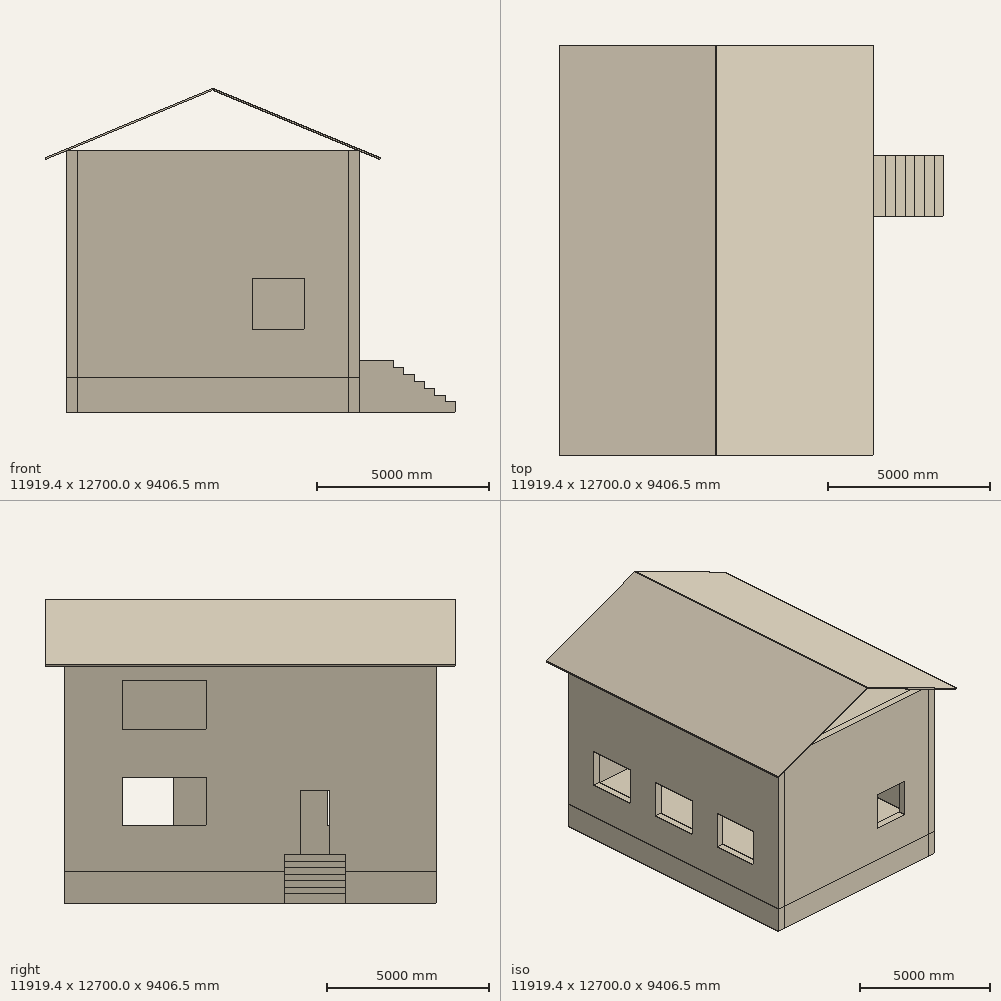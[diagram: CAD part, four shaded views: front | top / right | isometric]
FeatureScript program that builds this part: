
annotation { "Feature Type Name" : "Feature", "Feature Type Description" : "" }
export const myFeature = defineFeature(function(context is Context, id is Id, definition is map)
    precondition{}
    {
        {
            var Q0;
            Q0=qCreatedBy(makeId("Front.planeOp"),FACE);
            var sketch = newSketch(context, id + "F0", { "sketchPlane" : qUnion([Q0])});
            skLineSegment(sketch, "E0.bottom", {"start": v(0, 0) * mm, "end": v(300, 0) * mm});
            skLineSegment(sketch, "E0.top", {"start": v(0, 1000) * mm, "end": v(300, 1000) * mm});
            skLineSegment(sketch, "E0.left", {"start": v(0, 0) * mm, "end": v(0, 1000) * mm});
            skLineSegment(sketch, "E0.right", {"start": v(300, 0) * mm, "end": v(300, 1000) * mm});
            skSolve(sketch);
        }
        {
            var Q0;
            Q0 = qSketchRegion(id + "F0", true);
            extrude(context, id + "F1", {"entities" : qUnion([Q0]), "oppositeDirection" : true, "depth" : 11500 * mm});
        }
        {
            var Q0;
            Q0=makeQuery(id+"F1.opExtrude","SWEPT_BODY",BODY,{"disambiguationData":[OSD([sQuery(id+"F0.wireOp",EDGE,"E0.bottom"),sQuery(id+"F0.wireOp",EDGE,"E0.top"),sQuery(id+"F0.wireOp",EDGE,"E0.left"),sQuery(id+"F0.wireOp",EDGE,"E0.right")])]});
            transform(context, id + "F2", {"entities" : qUnion([Q0]), "transformType" : TransformType.TRANSLATION_3D, "dx" : 8200 * mm, "dy" : 0 * mm, "dz" : 0 * mm, "makeCopy" : true});
        }
        {
            var Q0;
            Q0=makeQuery(id+"F1.opExtrude","SWEPT_FACE",FACE,{"disambiguationData":[OSD([sQuery(id+"F0.wireOp",EDGE,"E0.right")])]});
            var sketch = newSketch(context, id + "F3", { "sketchPlane" : qUnion([Q0])});
            skLineSegment(sketch, "E1.bottom", {"start": v(0, 0) * mm, "end": v(300, 0) * mm});
            skLineSegment(sketch, "E1.top", {"start": v(0, 1000) * mm, "end": v(300, 1000) * mm});
            skLineSegment(sketch, "E1.left", {"start": v(0, 0) * mm, "end": v(0, 1000) * mm});
            skLineSegment(sketch, "E1.right", {"start": v(300, 0) * mm, "end": v(300, 1000) * mm});
            skSolve(sketch);
        }
        {
            var Q0;
            Q0 = qSketchRegion(id + "F3", true);
            extrude(context, id + "F4", {"entities" : qUnion([Q0]), "depth" : 7900 * mm});
        }
        {
            var Q0;
            Q0=makeQuery(id+"F4.opExtrude","SWEPT_BODY",BODY,{"disambiguationData":[OSD([sQuery(id+"F3.wireOp",EDGE,"E1.bottom"),sQuery(id+"F3.wireOp",EDGE,"E1.top"),sQuery(id+"F3.wireOp",EDGE,"E1.left"),sQuery(id+"F3.wireOp",EDGE,"E1.right")])]});
            transform(context, id + "F5", {"entities" : qUnion([Q0]), "transformType" : TransformType.TRANSLATION_3D, "dx" : 0 * mm, "dy" : 11200 * mm, "dz" : 0 * mm, "makeCopy" : true});
        }
        {
            var Q0;
            Q0=makeQuery(id+"F1.opExtrude","CAP_FACE",FACE,{"disambiguationData":[OSD([sQuery(id+"F0.wireOp",EDGE,"E0.bottom"),sQuery(id+"F0.wireOp",EDGE,"E0.top"),sQuery(id+"F0.wireOp",EDGE,"E0.left"),sQuery(id+"F0.wireOp",EDGE,"E0.right")])],"isStart":true});
            var sketch = newSketch(context, id + "F6", { "sketchPlane" : qUnion([Q0])});
            skLineSegment(sketch, "E2.bottom", {"start": v(0, 1000) * mm, "end": v(300, 1000) * mm});
            skLineSegment(sketch, "E2.top", {"start": v(0, 7600) * mm, "end": v(300, 7600) * mm});
            skLineSegment(sketch, "E2.left", {"start": v(0, 1000) * mm, "end": v(0, 7600) * mm});
            skLineSegment(sketch, "E2.right", {"start": v(300, 1000) * mm, "end": v(300, 7600) * mm});
            skSolve(sketch);
        }
        {
            var Q0;
            Q0=makeQuery(id+"F6.imprint","IMPRINT",FACE,{"disambiguationData":[TD([[makeQuery(id+"F6.imprint","IMPRINT",EDGE,{"derivedFrom":sQuery(id+"F6.wireOp",EDGE,"E2.bottom")}),1.0]])]});
            extrude(context, id + "F7", {"entities" : qUnion([Q0]), "oppositeDirection" : true, "depth" : 11500 * mm});
        }
        {
            var Q0;
            Q0=makeQuery(id+"F7.opExtrude","SWEPT_BODY",BODY,{"disambiguationData":[OSD([sQuery(id+"F6.wireOp",EDGE,"E2.bottom"),sQuery(id+"F6.wireOp",EDGE,"E2.top"),sQuery(id+"F6.wireOp",EDGE,"E2.left"),sQuery(id+"F6.wireOp",EDGE,"E2.right")])]});
            transform(context, id + "F8", {"entities" : qUnion([Q0]), "transformType" : TransformType.TRANSLATION_3D, "dx" : 8200 * mm, "dy" : 0 * mm, "dz" : 0 * mm, "makeCopy" : true});
        }
        {
            var Q0;
            Q0=makeQuery(id+"F7.opExtrude","SWEPT_FACE",FACE,{"disambiguationData":[OSD([sQuery(id+"F6.wireOp",EDGE,"E2.right")])]});
            var sketch = newSketch(context, id + "F9", { "sketchPlane" : qUnion([Q0])});
            skLineSegment(sketch, "E3.bottom", {"start": v(0, 1000) * mm, "end": v(300, 1000) * mm});
            skLineSegment(sketch, "E3.top", {"start": v(0, 7600) * mm, "end": v(300, 7600) * mm});
            skLineSegment(sketch, "E3.left", {"start": v(0, 1000) * mm, "end": v(0, 7600) * mm});
            skLineSegment(sketch, "E3.right", {"start": v(300, 1000) * mm, "end": v(300, 7600) * mm});
            skSolve(sketch);
        }
        {
            var Q0;
            Q0 = qSketchRegion(id + "F9", true);
            extrude(context, id + "F10", {"entities" : qUnion([Q0]), "depth" : 7900 * mm});
        }
        {
            var Q0;
            Q0=makeQuery(id+"F10.opExtrude","SWEPT_BODY",BODY,{"disambiguationData":[OSD([sQuery(id+"F9.wireOp",EDGE,"E3.bottom"),sQuery(id+"F9.wireOp",EDGE,"E3.top"),sQuery(id+"F9.wireOp",EDGE,"E3.left"),sQuery(id+"F9.wireOp",EDGE,"E3.right")])]});
            transform(context, id + "F11", {"entities" : qUnion([Q0]), "transformType" : TransformType.TRANSLATION_3D, "dx" : 0 * mm, "dy" : 11200 * mm, "dz" : 0 * mm, "makeCopy" : true});
        }
        {
            var Q0;
            Q0=makeQuery(id+"F8.opPattern","COPY",FACE,{"derivedFrom":makeQuery(id+"F7.opExtrude","SWEPT_FACE",FACE,{"disambiguationData":[OSD([sQuery(id+"F6.wireOp",EDGE,"E2.right")])]}),"instanceName":"1"});
            var sketch = newSketch(context, id + "F12", { "sketchPlane" : qUnion([Q0])});
            skLineSegment(sketch, "E4.bottom", {"start": v(0, 7600) * mm, "end": v(12700, 7600) * mm});
            skLineSegment(sketch, "E4.top", {"start": v(0, 7550) * mm, "end": v(12700, 7550) * mm});
            skLineSegment(sketch, "E4.left", {"start": v(0, 7600) * mm, "end": v(0, 7550) * mm});
            skLineSegment(sketch, "E4.right", {"start": v(12700, 7600) * mm, "end": v(12700, 7550) * mm});
            skSolve(sketch);
        }
        {
            var Q0;
            Q0 = qSketchRegion(id + "F12", true);
            extrude(context, id + "F13", {"entities" : qUnion([Q0]), "depth" : 650 * mm});
        }
        {
            var Q0;
            Q0=makeQuery(id+"F13.opExtrude","SWEPT_BODY",BODY,{"disambiguationData":[OSD([sQuery(id+"F12.wireOp",EDGE,"E4.bottom"),sQuery(id+"F12.wireOp",EDGE,"E4.top"),sQuery(id+"F12.wireOp",EDGE,"E4.left"),sQuery(id+"F12.wireOp",EDGE,"E4.right")])]});
            transform(context, id + "F14", {"entities" : qUnion([Q0]), "transformType" : TransformType.TRANSLATION_3D, "dx" : 0 * mm, "dy" : -600 * mm, "dz" : 0 * mm, "makeCopy" : false});
        }
        {
            var Q0;
            Q0=makeQuery(id+"F13.opExtrude","SWEPT_BODY",BODY,{"disambiguationData":[OSD([sQuery(id+"F12.wireOp",EDGE,"E4.bottom"),sQuery(id+"F12.wireOp",EDGE,"E4.top"),sQuery(id+"F12.wireOp",EDGE,"E4.left"),sQuery(id+"F12.wireOp",EDGE,"E4.right")])]});
            transform(context, id + "F15", {"entities" : qUnion([Q0]), "transformType" : TransformType.TRANSLATION_3D, "dx" : 0 * mm, "dy" : 0 * mm, "dz" : 50 * mm, "makeCopy" : false});
        }
        {
            var Q0;
            Q0=makeQuery(id+"F13.opExtrude","SWEPT_BODY",BODY,{"disambiguationData":[OSD([sQuery(id+"F12.wireOp",EDGE,"E4.bottom"),sQuery(id+"F12.wireOp",EDGE,"E4.top"),sQuery(id+"F12.wireOp",EDGE,"E4.left"),sQuery(id+"F12.wireOp",EDGE,"E4.right")])]});
            var Q1;
            Q1=makeQuery(id+"F8.opPattern","COPY",EDGE,{"derivedFrom":makeQuery(id+"F7.opExtrude","SWEPT_EDGE",EDGE,{"disambiguationData":[OSD([sQuery(id+"F6.wireOp",EDGE,"E2.top"),sQuery(id+"F6.wireOp",EDGE,"E2.right")])]}),"instanceName":"1"});
            transform(context, id + "F16", {"entities" : qUnion([Q0]), "transformType" : TransformType.ROTATION, "transformAxis" : qUnion([Q1]), "angle" : 22.5 * degree, "oppositeDirection" : true, "makeCopy" : false});
        }
        {
            var Q0;
            Q0=makeQuery(id+"F13.opExtrude","CAP_FACE",FACE,{"disambiguationData":[OSD([sQuery(id+"F12.wireOp",EDGE,"E4.bottom"),sQuery(id+"F12.wireOp",EDGE,"E4.top"),sQuery(id+"F12.wireOp",EDGE,"E4.left"),sQuery(id+"F12.wireOp",EDGE,"E4.right")])],"isStart":true});
            extrude(context, id + "F17", {"entities" : qUnion([Q0]), "operationType" : NewBodyOperationType.ADD, "depth" : 4600 * mm});
        }
        {
            var Q0;
            Q0=makeQuery(id+"F13.opExtrude","SWEPT_BODY",BODY,{"disambiguationData":[OSD([sQuery(id+"F12.wireOp",EDGE,"E4.bottom"),sQuery(id+"F12.wireOp",EDGE,"E4.top"),sQuery(id+"F12.wireOp",EDGE,"E4.left"),sQuery(id+"F12.wireOp",EDGE,"E4.right")])]});
            var Q1;
            {var subQ0=sQuery(id+"F12.wireOp",EDGE,"E4.right");var subQ1=sQuery(id+"F12.wireOp",EDGE,"E4.bottom");Q1=makeQuery(id+"F17.boolean.opBoolean","MERGE",EDGE,{"derivedFrom":[makeQuery(id+"F13.opExtrude","SWEPT_EDGE",EDGE,{"disambiguationData":[OSD([subQ1,subQ0])]}),makeQuery(id+"F17.opExtrude","SWEPT_EDGE",EDGE,{"disambiguationData":[OSD([subQ1,subQ0])]})]});}
            transform(context, id + "F18", {"entities" : qUnion([Q0]), "transformType" : TransformType.TRANSLATION_ENTITY, "oppositeDirectionEntity" : false, "transformLine" : qUnion([Q1]), "makeCopy" : true});
        }
        {
            var Q0;
            Q0=makeQuery(id+"F18.opPattern","COPY",BODY,{"derivedFrom":makeQuery(id+"F13.opExtrude","SWEPT_BODY",BODY,{"disambiguationData":[OSD([sQuery(id+"F12.wireOp",EDGE,"E4.bottom"),sQuery(id+"F12.wireOp",EDGE,"E4.top"),sQuery(id+"F12.wireOp",EDGE,"E4.left"),sQuery(id+"F12.wireOp",EDGE,"E4.right")])]}),"instanceName":"1"});
            var Q1;
            Q1=makeQuery(id+"F17.opExtrude","CAP_EDGE",EDGE,{"disambiguationData":[OSD([sQuery(id+"F12.wireOp",EDGE,"E4.top")])],"isStart":false});
            transform(context, id + "F19", {"entities" : qUnion([Q0]), "transformType" : TransformType.ROTATION, "transformAxis" : qUnion([Q1]), "angle" : 45 * degree, "oppositeDirection" : true, "makeCopy" : false});
        }
        {
            var Q0;
            Q0=makeQuery(id+"F8.opPattern","COPY",FACE,{"derivedFrom":makeQuery(id+"F7.opExtrude","SWEPT_FACE",FACE,{"disambiguationData":[OSD([sQuery(id+"F6.wireOp",EDGE,"E2.right")])]}),"instanceName":"1"});
            var sketch = newSketch(context, id + "F20", { "sketchPlane" : qUnion([Q0])});
            skLineSegment(sketch, "E5.bottom", {"start": v(0, 1000) * mm, "end": v(1800, 1000) * mm});
            skLineSegment(sketch, "E5.top", {"start": v(0, 2400) * mm, "end": v(1800, 2400) * mm});
            skLineSegment(sketch, "E5.left", {"start": v(0, 1000) * mm, "end": v(0, 2400) * mm});
            skLineSegment(sketch, "E5.right", {"start": v(1800, 1000) * mm, "end": v(1800, 2400) * mm});
            skSolve(sketch);
        }
        {
            var Q0;
            Q0 = qSketchRegion(id + "F20", true);
            extrude(context, id + "F21", {"entities" : qUnion([Q0]), "depth" : 25 * mm});
        }
        {
            var Q0;
            Q0=makeQuery(id+"F21.opExtrude","CAP_FACE",FACE,{"disambiguationData":[OSD([sQuery(id+"F20.wireOp",EDGE,"E5.bottom"),sQuery(id+"F20.wireOp",EDGE,"E5.top"),sQuery(id+"F20.wireOp",EDGE,"E5.left"),sQuery(id+"F20.wireOp",EDGE,"E5.right")])],"isStart":false});
            var sketch = newSketch(context, id + "F22", { "sketchPlane" : qUnion([Q0])});
            skLineSegment(sketch, "E6.bottom", {"start": v(1800, 2400) * mm, "end": v(4400, 2400) * mm});
            skLineSegment(sketch, "E6.top", {"start": v(1800, 3900) * mm, "end": v(4400, 3900) * mm});
            skLineSegment(sketch, "E6.left", {"start": v(1800, 2400) * mm, "end": v(1800, 3900) * mm});
            skLineSegment(sketch, "E6.right", {"start": v(4400, 2400) * mm, "end": v(4400, 3900) * mm});
            skSolve(sketch);
        }
        {
            var Q0;
            Q0=makeQuery(id+"F22.imprint","IMPRINT",FACE,{"disambiguationData":[TD([[makeQuery(id+"F22.imprint","IMPRINT",EDGE,{"derivedFrom":sQuery(id+"F22.wireOp",EDGE,"E6.bottom")}),1.0]])]});
            extrude(context, id + "F23", {"entities" : qUnion([Q0]), "operationType" : NewBodyOperationType.REMOVE, "oppositeDirection" : true, "depth" : 500 * mm});
        }
        {
            var Q0;
            Q0=makeQuery(id+"F21.opExtrude","SWEPT_BODY",BODY,{"disambiguationData":[OSD([sQuery(id+"F20.wireOp",EDGE,"E5.bottom"),sQuery(id+"F20.wireOp",EDGE,"E5.top"),sQuery(id+"F20.wireOp",EDGE,"E5.left"),sQuery(id+"F20.wireOp",EDGE,"E5.right")])]});
            deleteBodies(context, id + "F24", {"entities" : qUnion([Q0])});
        }
        {
            var Q0;
            Q0=makeQuery(id+"F8.opPattern","COPY",FACE,{"derivedFrom":makeQuery(id+"F7.opExtrude","SWEPT_FACE",FACE,{"disambiguationData":[OSD([sQuery(id+"F6.wireOp",EDGE,"E2.right")])]}),"instanceName":"1"});
            var sketch = newSketch(context, id + "F25", { "sketchPlane" : qUnion([Q0])});
            skLineSegment(sketch, "E7.bottom", {"start": v(0, 1000) * mm, "end": v(7300, 1000) * mm});
            skLineSegment(sketch, "E7.top", {"start": v(0, 1500) * mm, "end": v(7300, 1500) * mm});
            skLineSegment(sketch, "E7.left", {"start": v(0, 1000) * mm, "end": v(0, 1500) * mm});
            skLineSegment(sketch, "E7.right", {"start": v(7300, 1000) * mm, "end": v(7300, 1500) * mm});
            skSolve(sketch);
        }
        {
            var Q0;
            Q0 = qSketchRegion(id + "F25", true);
            extrude(context, id + "F26", {"entities" : qUnion([Q0]), "depth" : 25 * mm});
        }
        {
            var Q0;
            Q0=makeQuery(id+"F26.opExtrude","CAP_FACE",FACE,{"disambiguationData":[OSD([sQuery(id+"F25.wireOp",EDGE,"E7.bottom"),sQuery(id+"F25.wireOp",EDGE,"E7.top"),sQuery(id+"F25.wireOp",EDGE,"E7.left"),sQuery(id+"F25.wireOp",EDGE,"E7.right")])],"isStart":false});
            var sketch = newSketch(context, id + "F27", { "sketchPlane" : qUnion([Q0])});
            skLineSegment(sketch, "E8.bottom", {"start": v(7300, 1500) * mm, "end": v(8200, 1500) * mm});
            skLineSegment(sketch, "E8.top", {"start": v(7300, 3500) * mm, "end": v(8200, 3500) * mm});
            skLineSegment(sketch, "E8.left", {"start": v(7300, 1500) * mm, "end": v(7300, 3500) * mm});
            skLineSegment(sketch, "E8.right", {"start": v(8200, 1500) * mm, "end": v(8200, 3500) * mm});
            skSolve(sketch);
        }
        {
            var Q0;
            Q0=makeQuery(id+"F27.imprint","IMPRINT",FACE,{"disambiguationData":[TD([[makeQuery(id+"F27.imprint","IMPRINT",EDGE,{"derivedFrom":sQuery(id+"F27.wireOp",EDGE,"E8.bottom")}),1.0]])]});
            extrude(context, id + "F28", {"entities" : qUnion([Q0]), "operationType" : NewBodyOperationType.REMOVE, "oppositeDirection" : true, "depth" : 500 * mm});
        }
        {
            var Q0;
            Q0=makeQuery(id+"F26.opExtrude","SWEPT_BODY",BODY,{"disambiguationData":[OSD([sQuery(id+"F25.wireOp",EDGE,"E7.bottom"),sQuery(id+"F25.wireOp",EDGE,"E7.top"),sQuery(id+"F25.wireOp",EDGE,"E7.left"),sQuery(id+"F25.wireOp",EDGE,"E7.right")])]});
            deleteBodies(context, id + "F29", {"entities" : qUnion([Q0])});
        }
        {
            var Q0;
            Q0=makeQuery(id+"F8.opPattern","COPY",FACE,{"derivedFrom":makeQuery(id+"F7.opExtrude","SWEPT_FACE",FACE,{"disambiguationData":[OSD([sQuery(id+"F6.wireOp",EDGE,"E2.right")])]}),"instanceName":"1"});
            var sketch = newSketch(context, id + "F30", { "sketchPlane" : qUnion([Q0])});
            skLineSegment(sketch, "E9.bottom", {"start": v(7300, 1500) * mm, "end": v(9200, 1500) * mm});
            skLineSegment(sketch, "E9.top", {"start": v(7300, 0) * mm, "end": v(9200, 0) * mm});
            skLineSegment(sketch, "E9.left", {"start": v(7300, 1500) * mm, "end": v(7300, 0) * mm});
            skLineSegment(sketch, "E9.right", {"start": v(9200, 1500) * mm, "end": v(9200, 0) * mm});
            skSolve(sketch);
        }
        {
            var Q0;
            Q0 = qSketchRegion(id + "F30", true);
            extrude(context, id + "F31", {"entities" : qUnion([Q0]), "depth" : 1000 * mm});
        }
        {
            var Q0;
            Q0=makeQuery(id+"F31.opExtrude","SWEPT_BODY",BODY,{"disambiguationData":[OSD([sQuery(id+"F30.wireOp",EDGE,"E9.bottom"),sQuery(id+"F30.wireOp",EDGE,"E9.top"),sQuery(id+"F30.wireOp",EDGE,"E9.left"),sQuery(id+"F30.wireOp",EDGE,"E9.right")])]});
            transform(context, id + "F32", {"entities" : qUnion([Q0]), "transformType" : TransformType.TRANSLATION_3D, "dx" : 0 * mm, "dy" : -500 * mm, "dz" : 0 * mm, "makeCopy" : false});
        }
        {
            var Q0;
            Q0=makeQuery(id+"F31.opExtrude","CAP_FACE",FACE,{"disambiguationData":[OSD([sQuery(id+"F30.wireOp",EDGE,"E9.bottom"),sQuery(id+"F30.wireOp",EDGE,"E9.top"),sQuery(id+"F30.wireOp",EDGE,"E9.left"),sQuery(id+"F30.wireOp",EDGE,"E9.right")])],"isStart":false});
            var sketch = newSketch(context, id + "F33", { "sketchPlane" : qUnion([Q0])});
            skLineSegment(sketch, "E10.bottom", {"start": v(6800, 0) * mm, "end": v(8700, 0) * mm});
            skLineSegment(sketch, "E10.top", {"start": v(6800, 1300) * mm, "end": v(8700, 1300) * mm});
            skLineSegment(sketch, "E10.left", {"start": v(6800, 0) * mm, "end": v(6800, 1300) * mm});
            skLineSegment(sketch, "E10.right", {"start": v(8700, 0) * mm, "end": v(8700, 1300) * mm});
            skSolve(sketch);
        }
        {
            var Q0;
            Q0 = qSketchRegion(id + "F33", true);
            extrude(context, id + "F34", {"entities" : qUnion([Q0]), "operationType" : NewBodyOperationType.ADD, "depth" : 300 * mm});
        }
        {
            var Q0;
            Q0=makeQuery(id+"F34.opExtrude","CAP_FACE",FACE,{"disambiguationData":[OSD([sQuery(id+"F33.wireOp",EDGE,"E10.bottom"),sQuery(id+"F33.wireOp",EDGE,"E10.top"),sQuery(id+"F33.wireOp",EDGE,"E10.left"),sQuery(id+"F33.wireOp",EDGE,"E10.right")])],"isStart":false});
            var sketch = newSketch(context, id + "F35", { "sketchPlane" : qUnion([Q0])});
            skLineSegment(sketch, "E11.bottom", {"start": v(6800, 0) * mm, "end": v(8700, 0) * mm});
            skLineSegment(sketch, "E11.top", {"start": v(6800, 1100) * mm, "end": v(8700, 1100) * mm});
            skLineSegment(sketch, "E11.left", {"start": v(6800, 0) * mm, "end": v(6800, 1100) * mm});
            skLineSegment(sketch, "E11.right", {"start": v(8700, 0) * mm, "end": v(8700, 1100) * mm});
            skSolve(sketch);
        }
        {
            var Q0;
            Q0 = qSketchRegion(id + "F35", true);
            extrude(context, id + "F36", {"entities" : qUnion([Q0]), "operationType" : NewBodyOperationType.ADD, "depth" : 300 * mm});
        }
        {
            var Q0;
            Q0=makeQuery(id+"F36.opExtrude","CAP_FACE",FACE,{"disambiguationData":[OSD([sQuery(id+"F35.wireOp",EDGE,"E11.bottom"),sQuery(id+"F35.wireOp",EDGE,"E11.top"),sQuery(id+"F35.wireOp",EDGE,"E11.left"),sQuery(id+"F35.wireOp",EDGE,"E11.right")])],"isStart":false});
            var sketch = newSketch(context, id + "F37", { "sketchPlane" : qUnion([Q0])});
            skLineSegment(sketch, "E12.bottom", {"start": v(6800, 0) * mm, "end": v(8700, 0) * mm});
            skLineSegment(sketch, "E12.top", {"start": v(6800, 900) * mm, "end": v(8700, 900) * mm});
            skLineSegment(sketch, "E12.left", {"start": v(6800, 0) * mm, "end": v(6800, 900) * mm});
            skLineSegment(sketch, "E12.right", {"start": v(8700, 0) * mm, "end": v(8700, 900) * mm});
            skSolve(sketch);
        }
        {
            var Q0;
            Q0 = qSketchRegion(id + "F37", true);
            extrude(context, id + "F38", {"entities" : qUnion([Q0]), "operationType" : NewBodyOperationType.ADD, "depth" : 300 * mm});
        }
        {
            var Q0;
            Q0=makeQuery(id+"F38.opExtrude","CAP_FACE",FACE,{"disambiguationData":[OSD([sQuery(id+"F37.wireOp",EDGE,"E12.bottom"),sQuery(id+"F37.wireOp",EDGE,"E12.top"),sQuery(id+"F37.wireOp",EDGE,"E12.left"),sQuery(id+"F37.wireOp",EDGE,"E12.right")])],"isStart":false});
            var sketch = newSketch(context, id + "F39", { "sketchPlane" : qUnion([Q0])});
            skLineSegment(sketch, "E13.bottom", {"start": v(6800, 0) * mm, "end": v(8700, 0) * mm});
            skLineSegment(sketch, "E13.top", {"start": v(6800, 700) * mm, "end": v(8700, 700) * mm});
            skLineSegment(sketch, "E13.left", {"start": v(6800, 0) * mm, "end": v(6800, 700) * mm});
            skLineSegment(sketch, "E13.right", {"start": v(8700, 0) * mm, "end": v(8700, 700) * mm});
            skSolve(sketch);
        }
        {
            var Q0;
            Q0 = qSketchRegion(id + "F39", true);
            extrude(context, id + "F40", {"entities" : qUnion([Q0]), "operationType" : NewBodyOperationType.ADD, "depth" : 300 * mm});
        }
        {
            var Q0;
            Q0=makeQuery(id+"F40.opExtrude","CAP_FACE",FACE,{"disambiguationData":[OSD([sQuery(id+"F39.wireOp",EDGE,"E13.bottom"),sQuery(id+"F39.wireOp",EDGE,"E13.top"),sQuery(id+"F39.wireOp",EDGE,"E13.left"),sQuery(id+"F39.wireOp",EDGE,"E13.right")])],"isStart":false});
            var sketch = newSketch(context, id + "F41", { "sketchPlane" : qUnion([Q0])});
            skLineSegment(sketch, "E14.bottom", {"start": v(6800, 0) * mm, "end": v(8700, 0) * mm});
            skLineSegment(sketch, "E14.top", {"start": v(6800, 500) * mm, "end": v(8700, 500) * mm});
            skLineSegment(sketch, "E14.left", {"start": v(6800, 0) * mm, "end": v(6800, 500) * mm});
            skLineSegment(sketch, "E14.right", {"start": v(8700, 0) * mm, "end": v(8700, 500) * mm});
            skSolve(sketch);
        }
        {
            var Q0;
            Q0 = qSketchRegion(id + "F41", true);
            extrude(context, id + "F42", {"entities" : qUnion([Q0]), "operationType" : NewBodyOperationType.ADD, "depth" : 300 * mm});
        }
        {
            var Q0;
            Q0=makeQuery(id+"F42.opExtrude","CAP_FACE",FACE,{"disambiguationData":[OSD([sQuery(id+"F41.wireOp",EDGE,"E14.bottom"),sQuery(id+"F41.wireOp",EDGE,"E14.top"),sQuery(id+"F41.wireOp",EDGE,"E14.left"),sQuery(id+"F41.wireOp",EDGE,"E14.right")])],"isStart":false});
            var sketch = newSketch(context, id + "F43", { "sketchPlane" : qUnion([Q0])});
            skLineSegment(sketch, "E15.bottom", {"start": v(6800, 0) * mm, "end": v(8700, 0) * mm});
            skLineSegment(sketch, "E15.top", {"start": v(6800, 300) * mm, "end": v(8700, 300) * mm});
            skLineSegment(sketch, "E15.left", {"start": v(6800, 0) * mm, "end": v(6800, 300) * mm});
            skLineSegment(sketch, "E15.right", {"start": v(8700, 0) * mm, "end": v(8700, 300) * mm});
            skSolve(sketch);
        }
        {
            var Q0;
            Q0 = qSketchRegion(id + "F43", true);
            extrude(context, id + "F44", {"entities" : qUnion([Q0]), "operationType" : NewBodyOperationType.ADD, "depth" : 300 * mm});
        }
        {
            var Q0;
            Q0=makeQuery(id+"F10.opExtrude","SWEPT_FACE",FACE,{"disambiguationData":[OSD([sQuery(id+"F9.wireOp",EDGE,"E3.left")])]});
            var sketch = newSketch(context, id + "F45", { "sketchPlane" : qUnion([Q0])});
            skLineSegment(sketch, "E16.bottom", {"start": v(8200, 1000) * mm, "end": v(6900, 1000) * mm});
            skLineSegment(sketch, "E16.top", {"start": v(8200, 2400) * mm, "end": v(6900, 2400) * mm});
            skLineSegment(sketch, "E16.left", {"start": v(8200, 1000) * mm, "end": v(8200, 2400) * mm});
            skLineSegment(sketch, "E16.right", {"start": v(6900, 1000) * mm, "end": v(6900, 2400) * mm});
            skSolve(sketch);
        }
        {
            var Q0;
            Q0 = qSketchRegion(id + "F45", true);
            extrude(context, id + "F46", {"entities" : qUnion([Q0]), "depth" : 25 * mm});
        }
        {
            var Q0;
            Q0=makeQuery(id+"F46.opExtrude","CAP_FACE",FACE,{"disambiguationData":[OSD([sQuery(id+"F45.wireOp",EDGE,"E16.bottom"),sQuery(id+"F45.wireOp",EDGE,"E16.top"),sQuery(id+"F45.wireOp",EDGE,"E16.left"),sQuery(id+"F45.wireOp",EDGE,"E16.right")])],"isStart":false});
            var sketch = newSketch(context, id + "F47", { "sketchPlane" : qUnion([Q0])});
            skLineSegment(sketch, "E17.bottom", {"start": v(6900, 2400) * mm, "end": v(5400, 2400) * mm});
            skLineSegment(sketch, "E17.top", {"start": v(6900, 3900) * mm, "end": v(5400, 3900) * mm});
            skLineSegment(sketch, "E17.left", {"start": v(6900, 2400) * mm, "end": v(6900, 3900) * mm});
            skLineSegment(sketch, "E17.right", {"start": v(5400, 2400) * mm, "end": v(5400, 3900) * mm});
            skSolve(sketch);
        }
        {
            var Q0;
            Q0 = qSketchRegion(id + "F47", true);
            extrude(context, id + "F48", {"entities" : qUnion([Q0]), "operationType" : NewBodyOperationType.REMOVE, "oppositeDirection" : true, "depth" : 500 * mm});
        }
        {
            var Q0;
            Q0=makeQuery(id+"F46.opExtrude","SWEPT_BODY",BODY,{"disambiguationData":[OSD([sQuery(id+"F45.wireOp",EDGE,"E16.bottom"),sQuery(id+"F45.wireOp",EDGE,"E16.top"),sQuery(id+"F45.wireOp",EDGE,"E16.left"),sQuery(id+"F45.wireOp",EDGE,"E16.right")])]});
            deleteBodies(context, id + "F49", {"entities" : qUnion([Q0])});
        }
        {
            var Q0;
            Q0=makeQuery(id+"F7.opExtrude","SWEPT_FACE",FACE,{"disambiguationData":[OSD([sQuery(id+"F6.wireOp",EDGE,"E2.left")])]});
            var sketch = newSketch(context, id + "F50", { "sketchPlane" : qUnion([Q0])});
            skLineSegment(sketch, "E18.bottom", {"start": v(-11500, 1000) * mm, "end": v(-10125, 1000) * mm});
            skLineSegment(sketch, "E18.top", {"start": v(-11500, 2400) * mm, "end": v(-10125, 2400) * mm});
            skLineSegment(sketch, "E18.left", {"start": v(-11500, 1000) * mm, "end": v(-11500, 2400) * mm});
            skLineSegment(sketch, "E18.right", {"start": v(-10125, 1000) * mm, "end": v(-10125, 2400) * mm});
            skSolve(sketch);
        }
        {
            var Q0;
            Q0 = qSketchRegion(id + "F50", true);
            extrude(context, id + "F51", {"entities" : qUnion([Q0]), "depth" : 25 * mm});
        }
        {
            var Q0;
            Q0=makeQuery(id+"F51.opExtrude","CAP_FACE",FACE,{"disambiguationData":[OSD([sQuery(id+"F50.wireOp",EDGE,"E18.bottom"),sQuery(id+"F50.wireOp",EDGE,"E18.top"),sQuery(id+"F50.wireOp",EDGE,"E18.left"),sQuery(id+"F50.wireOp",EDGE,"E18.right")])],"isStart":false});
            var sketch = newSketch(context, id + "F52", { "sketchPlane" : qUnion([Q0])});
            skLineSegment(sketch, "E19.bottom", {"start": v(-10125, 2400) * mm, "end": v(-8125, 2400) * mm});
            skLineSegment(sketch, "E19.top", {"start": v(-10125, 3900) * mm, "end": v(-8125, 3900) * mm});
            skLineSegment(sketch, "E19.left", {"start": v(-10125, 2400) * mm, "end": v(-10125, 3900) * mm});
            skLineSegment(sketch, "E19.right", {"start": v(-8125, 2400) * mm, "end": v(-8125, 3900) * mm});
            skSolve(sketch);
        }
        {
            var Q0;
            Q0 = qSketchRegion(id + "F52", true);
            extrude(context, id + "F53", {"entities" : qUnion([Q0]), "operationType" : NewBodyOperationType.REMOVE, "oppositeDirection" : true, "depth" : 500 * mm});
        }
        {
            var Q0;
            Q0=makeQuery(id+"F51.opExtrude","SWEPT_BODY",BODY,{"disambiguationData":[OSD([sQuery(id+"F50.wireOp",EDGE,"E18.bottom"),sQuery(id+"F50.wireOp",EDGE,"E18.top"),sQuery(id+"F50.wireOp",EDGE,"E18.left"),sQuery(id+"F50.wireOp",EDGE,"E18.right")])]});
            deleteBodies(context, id + "F54", {"entities" : qUnion([Q0])});
        }
        {
            var Q0;
            Q0=makeQuery(id+"F7.opExtrude","SWEPT_FACE",FACE,{"disambiguationData":[OSD([sQuery(id+"F6.wireOp",EDGE,"E2.left")])]});
            var sketch = newSketch(context, id + "F55", { "sketchPlane" : qUnion([Q0])});
            skLineSegment(sketch, "E20.bottom", {"start": v(-11500, 1000) * mm, "end": v(-6750, 1000) * mm});
            skLineSegment(sketch, "E20.top", {"start": v(-11500, 2400) * mm, "end": v(-6750, 2400) * mm});
            skLineSegment(sketch, "E20.left", {"start": v(-11500, 1000) * mm, "end": v(-11500, 2400) * mm});
            skLineSegment(sketch, "E20.right", {"start": v(-6750, 1000) * mm, "end": v(-6750, 2400) * mm});
            skSolve(sketch);
        }
        {
            var Q0;
            Q0 = qSketchRegion(id + "F55", true);
            extrude(context, id + "F56", {"entities" : qUnion([Q0]), "depth" : 25 * mm});
        }
        {
            var Q0;
            Q0=makeQuery(id+"F56.opExtrude","CAP_FACE",FACE,{"disambiguationData":[OSD([sQuery(id+"F55.wireOp",EDGE,"E20.bottom"),sQuery(id+"F55.wireOp",EDGE,"E20.top"),sQuery(id+"F55.wireOp",EDGE,"E20.left"),sQuery(id+"F55.wireOp",EDGE,"E20.right")])],"isStart":false});
            var sketch = newSketch(context, id + "F57", { "sketchPlane" : qUnion([Q0])});
            skLineSegment(sketch, "E21.bottom", {"start": v(-6750, 2400) * mm, "end": v(-4750, 2400) * mm});
            skLineSegment(sketch, "E21.top", {"start": v(-6750, 3900) * mm, "end": v(-4750, 3900) * mm});
            skLineSegment(sketch, "E21.left", {"start": v(-6750, 2400) * mm, "end": v(-6750, 3900) * mm});
            skLineSegment(sketch, "E21.right", {"start": v(-4750, 2400) * mm, "end": v(-4750, 3900) * mm});
            skSolve(sketch);
        }
        {
            var Q0;
            Q0 = qSketchRegion(id + "F57", true);
            extrude(context, id + "F58", {"entities" : qUnion([Q0]), "operationType" : NewBodyOperationType.REMOVE, "oppositeDirection" : true, "depth" : 500 * mm});
        }
        {
            var Q0;
            Q0=makeQuery(id+"F56.opExtrude","SWEPT_BODY",BODY,{"disambiguationData":[OSD([sQuery(id+"F55.wireOp",EDGE,"E20.bottom"),sQuery(id+"F55.wireOp",EDGE,"E20.top"),sQuery(id+"F55.wireOp",EDGE,"E20.left"),sQuery(id+"F55.wireOp",EDGE,"E20.right")])]});
            deleteBodies(context, id + "F59", {"entities" : qUnion([Q0])});
        }
        {
            var Q0;
            Q0=makeQuery(id+"F7.opExtrude","SWEPT_FACE",FACE,{"disambiguationData":[OSD([sQuery(id+"F6.wireOp",EDGE,"E2.left")])]});
            var sketch = newSketch(context, id + "F60", { "sketchPlane" : qUnion([Q0])});
            skLineSegment(sketch, "E22.bottom", {"start": v(-11500, 1000) * mm, "end": v(-3375, 1000) * mm});
            skLineSegment(sketch, "E22.top", {"start": v(-11500, 2400) * mm, "end": v(-3375, 2400) * mm});
            skLineSegment(sketch, "E22.left", {"start": v(-11500, 1000) * mm, "end": v(-11500, 2400) * mm});
            skLineSegment(sketch, "E22.right", {"start": v(-3375, 1000) * mm, "end": v(-3375, 2400) * mm});
            skSolve(sketch);
        }
        {
            var Q0;
            Q0 = qSketchRegion(id + "F60", true);
            extrude(context, id + "F61", {"entities" : qUnion([Q0]), "depth" : 25 * mm});
        }
        {
            var Q0;
            Q0=makeQuery(id+"F61.opExtrude","CAP_FACE",FACE,{"disambiguationData":[OSD([sQuery(id+"F60.wireOp",EDGE,"E22.bottom"),sQuery(id+"F60.wireOp",EDGE,"E22.top"),sQuery(id+"F60.wireOp",EDGE,"E22.left"),sQuery(id+"F60.wireOp",EDGE,"E22.right")])],"isStart":false});
            var sketch = newSketch(context, id + "F62", { "sketchPlane" : qUnion([Q0])});
            skLineSegment(sketch, "E23.bottom", {"start": v(-3375, 2400) * mm, "end": v(-1375, 2400) * mm});
            skLineSegment(sketch, "E23.top", {"start": v(-3375, 3900) * mm, "end": v(-1375, 3900) * mm});
            skLineSegment(sketch, "E23.left", {"start": v(-3375, 2400) * mm, "end": v(-3375, 3900) * mm});
            skLineSegment(sketch, "E23.right", {"start": v(-1375, 2400) * mm, "end": v(-1375, 3900) * mm});
            skSolve(sketch);
        }
        {
            var Q0;
            Q0 = qSketchRegion(id + "F62", true);
            extrude(context, id + "F63", {"entities" : qUnion([Q0]), "operationType" : NewBodyOperationType.REMOVE, "oppositeDirection" : true, "depth" : 500 * mm});
        }
        {
            var Q0;
            Q0=makeQuery(id+"F61.opExtrude","SWEPT_BODY",BODY,{"disambiguationData":[OSD([sQuery(id+"F60.wireOp",EDGE,"E22.bottom"),sQuery(id+"F60.wireOp",EDGE,"E22.top"),sQuery(id+"F60.wireOp",EDGE,"E22.left"),sQuery(id+"F60.wireOp",EDGE,"E22.right")])]});
            deleteBodies(context, id + "F64", {"entities" : qUnion([Q0])});
        }
        {
            var Q0;
            Q0=makeQuery(id+"F10.opExtrude","SWEPT_FACE",FACE,{"disambiguationData":[OSD([sQuery(id+"F9.wireOp",EDGE,"E3.right")])]});
            var sketch = newSketch(context, id + "F65", { "sketchPlane" : qUnion([Q0])});
            skLineSegment(sketch, "E24.bottom", {"start": v(-300, 1000) * mm, "end": v(-8200, 1000) * mm});
            skLineSegment(sketch, "E24.top", {"start": v(-300, 1500) * mm, "end": v(-8200, 1500) * mm});
            skLineSegment(sketch, "E24.left", {"start": v(-300, 1000) * mm, "end": v(-300, 1500) * mm});
            skLineSegment(sketch, "E24.right", {"start": v(-8200, 1000) * mm, "end": v(-8200, 1500) * mm});
            skSolve(sketch);
        }
        {
            var Q0;
            Q0 = qSketchRegion(id + "F65", true);
            extrude(context, id + "F66", {"entities" : qUnion([Q0]), "endBound" : BoundingType.UP_TO_NEXT, "depth" : 25 * mm});
        }
        {
            var Q0;
            Q0=makeQuery(id+"F66.opExtrude","SWEPT_FACE",FACE,{"disambiguationData":[OSD([sQuery(id+"F65.wireOp",EDGE,"E24.top")])]});
            var sketch = newSketch(context, id + "F67", { "sketchPlane" : qUnion([Q0])});
            skLineSegment(sketch, "E25.bottom", {"start": v(300, 11200) * mm, "end": v(8200, 11200) * mm});
            skLineSegment(sketch, "E25.top", {"start": v(300, 300) * mm, "end": v(8200, 300) * mm});
            skLineSegment(sketch, "E25.left", {"start": v(300, 11200) * mm, "end": v(300, 300) * mm});
            skLineSegment(sketch, "E25.right", {"start": v(8200, 11200) * mm, "end": v(8200, 300) * mm});
            skSolve(sketch);
        }
        {
            var Q0;
            Q0 = qSketchRegion(id + "F67", true);
            extrude(context, id + "F68", {"entities" : qUnion([Q0]), "depth" : 300 * mm});
        }
        {
            var Q0;
            Q0=makeQuery(id+"F68.opExtrude","SWEPT_BODY",BODY,{"disambiguationData":[OSD([sQuery(id+"F67.wireOp",EDGE,"E25.bottom"),sQuery(id+"F67.wireOp",EDGE,"E25.top"),sQuery(id+"F67.wireOp",EDGE,"E25.left"),sQuery(id+"F67.wireOp",EDGE,"E25.right")])]});
            transform(context, id + "F69", {"entities" : qUnion([Q0]), "transformType" : TransformType.TRANSLATION_3D, "dx" : 0 * mm, "dy" : 0 * mm, "dz" : 2700 * mm, "makeCopy" : false});
        }
        {
            var Q0;
            Q0=makeQuery(id+"F8.opPattern","COPY",FACE,{"derivedFrom":makeQuery(id+"F7.opExtrude","SWEPT_FACE",FACE,{"disambiguationData":[OSD([sQuery(id+"F6.wireOp",EDGE,"E2.right")])]}),"instanceName":"1"});
            var sketch = newSketch(context, id + "F70", { "sketchPlane" : qUnion([Q0])});
            skLineSegment(sketch, "E26.bottom", {"start": v(1800, 2400) * mm, "end": v(4400, 2400) * mm});
            skLineSegment(sketch, "E26.top", {"start": v(1800, 3900) * mm, "end": v(4400, 3900) * mm});
            skLineSegment(sketch, "E26.left", {"start": v(1800, 2400) * mm, "end": v(1800, 3900) * mm});
            skLineSegment(sketch, "E26.right", {"start": v(4400, 2400) * mm, "end": v(4400, 3900) * mm});
            skSolve(sketch);
        }
        {
            var Q0;
            Q0 = qSketchRegion(id + "F70", true);
            extrude(context, id + "F71", {"entities" : qUnion([Q0]), "depth" : 25 * mm});
        }
        {
            var Q0;
            Q0=makeQuery(id+"F71.opExtrude","SWEPT_BODY",BODY,{"disambiguationData":[OSD([sQuery(id+"F70.wireOp",EDGE,"E26.bottom"),sQuery(id+"F70.wireOp",EDGE,"E26.top"),sQuery(id+"F70.wireOp",EDGE,"E26.left"),sQuery(id+"F70.wireOp",EDGE,"E26.right")])]});
            transform(context, id + "F72", {"entities" : qUnion([Q0]), "transformType" : TransformType.TRANSLATION_3D, "dx" : 0 * mm, "dy" : 0 * mm, "dz" : 3000 * mm, "makeCopy" : false});
        }
        {
            var Q0;
            Q0=makeQuery(id+"F71.opExtrude","CAP_FACE",FACE,{"disambiguationData":[OSD([sQuery(id+"F70.wireOp",EDGE,"E26.bottom"),sQuery(id+"F70.wireOp",EDGE,"E26.top"),sQuery(id+"F70.wireOp",EDGE,"E26.left"),sQuery(id+"F70.wireOp",EDGE,"E26.right")])],"isStart":false});
            extrude(context, id + "F73", {"entities" : qUnion([Q0]), "operationType" : NewBodyOperationType.REMOVE, "oppositeDirection" : true, "depth" : 500 * mm});
        }
        {
            var Q0;
            Q0=makeQuery(id+"F66.opExtrude","SWEPT_BODY",BODY,{"disambiguationData":[OSD([sQuery(id+"F65.wireOp",EDGE,"E24.bottom"),sQuery(id+"F65.wireOp",EDGE,"E24.top"),sQuery(id+"F65.wireOp",EDGE,"E24.left"),sQuery(id+"F65.wireOp",EDGE,"E24.right")])]});
            transform(context, id + "F74", {"entities" : qUnion([Q0]), "transformType" : TransformType.TRANSLATION_3D, "dx" : 0 * mm, "dy" : 0 * mm, "dz" : 6000 * mm, "makeCopy" : true});
        }
    });
